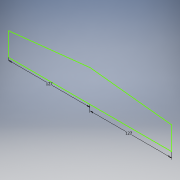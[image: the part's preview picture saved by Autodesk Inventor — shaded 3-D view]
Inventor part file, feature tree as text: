
AUTODESK INVENTOR PART (.ipt)
format: ipt  version: 2018 (Build 220112000, 112)  size: 89,088 bytes
history: native  units: in
note: dims shown in document units (in); Inventor stores cm internally (conversion verified against a paired STEP export)
features: sketch x1
ambient origin geometry x8: Origin, YZ Plane, XZ Plane, XY Plane, X Axis, Y Axis, Z Axis, Center Point
feature tree (1):
  sketch  "Sketch2"  dims[d5=5.0in d6=5.0in]
